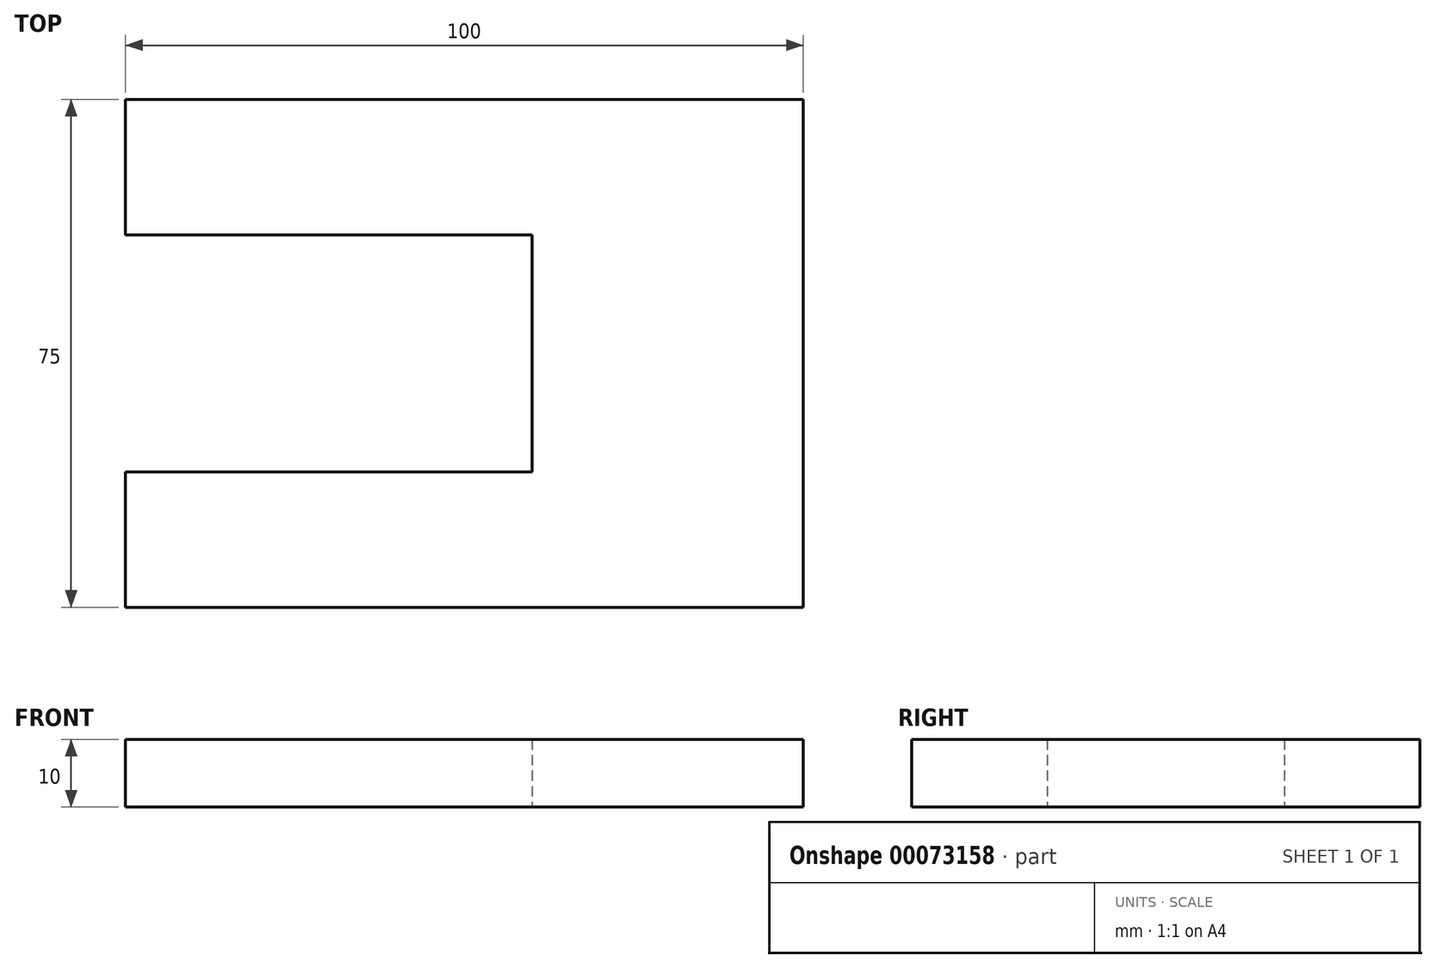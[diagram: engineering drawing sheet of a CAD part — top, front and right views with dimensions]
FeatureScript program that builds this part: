
annotation { "Feature Type Name" : "Feature", "Feature Type Description" : "" }
export const myFeature = defineFeature(function(context is Context, id is Id, definition is map)
    precondition{}
    {
        {
            var Q0;
            Q0=qCreatedBy(makeId("Top.planeOp"),FACE);
            var sketch = newSketch(context, id + "F0", { "sketchPlane" : qUnion([Q0])});
            skLineSegment(sketch, "E0.bottom", {"start": v(0, 0) * mm, "end": v(100, 0) * mm});
            skLineSegment(sketch, "E0.top", {"start": v(0, 75) * mm, "end": v(100, 75) * mm});
            skLineSegment(sketch, "E0.left", {"start": v(0, 0) * mm, "end": v(0, 75) * mm});
            skLineSegment(sketch, "E0.right", {"start": v(100, 0) * mm, "end": v(100, 75) * mm});
            skLineSegment(sketch, "E1", {"start": v(0, 55) * mm, "end": v(100, 55) * mm});
            skLineSegment(sketch, "E2", {"start": v(0, 20) * mm, "end": v(100, 20) * mm});
            skLineSegment(sketch, "E3", {"start": v(60, 55) * mm, "end": v(60, 20) * mm});
            skSolve(sketch);
        }
        {
            var Q0;
            {var subQ4=sQuery(id+"F0.wireOp",EDGE,"E0.top");Q0=makeQuery(id+"F0.imprint","IMPRINT",FACE,{"disambiguationData":[TD([[makeQuery(id+"F0.imprint","IMPRINT",EDGE,{"derivedFrom":subQ4}),-1.0]])]});}
            var Q1;
            {var subQ5=sQuery(id+"F0.wireOp",EDGE,"E3");Q1=makeQuery(id+"F0.imprint","IMPRINT",FACE,{"disambiguationData":[TD([[makeQuery(id+"F0.imprint","IMPRINT",EDGE,{"derivedFrom":subQ5}),1.0]])]});}
            var Q2;
            {var subQ5=sQuery(id+"F0.wireOp",EDGE,"E0.bottom");Q2=makeQuery(id+"F0.imprint","IMPRINT",FACE,{"disambiguationData":[TD([[makeQuery(id+"F0.imprint","IMPRINT",EDGE,{"derivedFrom":subQ5}),1.0]])]});}
            extrude(context, id + "F1", {"entities" : qUnion([Q0, Q1, Q2]), "depth" : 10 * mm});
        }
        {
            var Q0;
            Q0=makeQuery(id+"F1.opExtrude","CAP_FACE",FACE,{"disambiguationData":[OSD([sQuery(id+"F0.wireOp",EDGE,"E0.bottom"),sQuery(id+"F0.wireOp",EDGE,"E0.top"),sQuery(id+"F0.wireOp",EDGE,"E0.left"),sQuery(id+"F0.wireOp",EDGE,"E0.right"),sQuery(id+"F0.wireOp",EDGE,"E1"),sQuery(id+"F0.wireOp",EDGE,"E2"),sQuery(id+"F0.wireOp",EDGE,"E3")])],"isStart":false});
            var sketch = newSketch(context, id + "F2", { "sketchPlane" : qUnion([Q0])});
            skArc(sketch, "E4", {"start": v(0, 7) * mm, "mid": v(6.78, 1.95) * mm, "end": v(15, 0) * mm});
            skArc(sketch, "E5", {"start": v(15, 75) * mm, "mid": v(6.97, 72.63) * mm, "end": v(0, 68) * mm});
            skSolve(sketch);
        }
        {
            var Q0;
            {var subQ0=sQuery(id+"F2.wireOp",EDGE,"E5");Q0=makeQuery(id+"F2.imprint","IMPRINT",FACE,{"disambiguationData":[TD([[makeQuery(id+"F2.imprint","IMPRINT",EDGE,{"derivedFrom":subQ0}),-1.0]])]});}
            var Q1;
            {var subQ0=sQuery(id+"F2.wireOp",EDGE,"E4");Q1=makeQuery(id+"F2.imprint","IMPRINT",FACE,{"disambiguationData":[TD([[makeQuery(id+"F2.imprint","IMPRINT",EDGE,{"derivedFrom":subQ0}),-1.0]])]});}
            extrude(context, id + "F3", {"entities" : qUnion([Q0, Q1]), "operationType" : NewBodyOperationType.ADD, "endBound" : BoundingType.UP_TO_NEXT, "oppositeDirection" : true, "depth" : 10 * mm});
        }
    });
